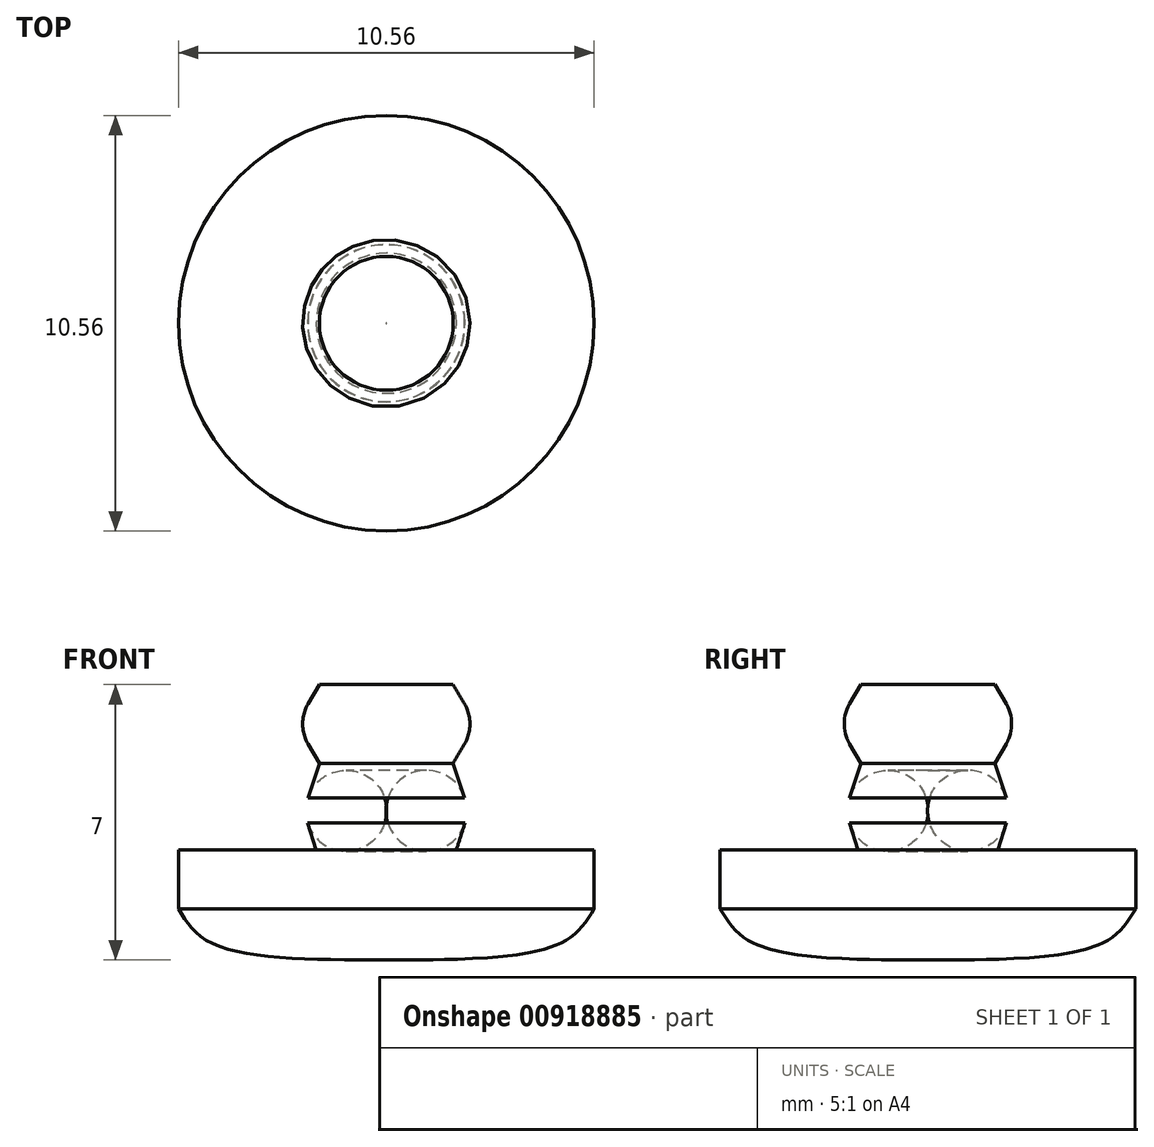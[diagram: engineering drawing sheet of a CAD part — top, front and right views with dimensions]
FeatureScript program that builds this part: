
annotation { "Feature Type Name" : "Feature", "Feature Type Description" : "" }
export const myFeature = defineFeature(function(context is Context, id is Id, definition is map)
    precondition{}
    {
        {
            var Q0;
            Q0=qCreatedBy(makeId("Front.planeOp"),FACE);
            var sketch = newSketch(context, id + "F0", { "sketchPlane" : qUnion([Q0])});
            skLineSegment(sketch, "E0", {"start": v(-34, -22) * mm, "end": v(-34.29, -22.5) * mm});
            skLineSegment(sketch, "E1", {"start": v(-34.29, -23.5) * mm, "end": v(-34, -24) * mm});
            skPoint(sketch, "E2.visualSharp", {"position": v(-34.59, -23) * mm});
            skArc(sketch, "E2.filletArc", {"start": v(-34.29, -22.5) * mm, "mid": v(-34.43, -23) * mm, "end": v(-34.29, -23.5) * mm});
            skLineSegment(sketch, "E3", {"start": v(-34, -24) * mm, "end": v(-34.3, -24.88) * mm});
            skLineSegment(sketch, "E4", {"start": v(-34.3, -25.52) * mm, "end": v(-34.08, -26.2) * mm});
            skPoint(sketch, "E5.visualSharp", {"position": v(-34.4, -25.2) * mm});
            skArc(sketch, "E5.filletArc", {"start": v(-34.3, -24.88) * mm, "mid": v(-34.35, -25.2) * mm, "end": v(-34.3, -25.52) * mm});
            skLineSegment(sketch, "E6", {"start": v(-34.08, -26.2) * mm, "end": v(-37.58, -26.2) * mm});
            skLineSegment(sketch, "E7", {"start": v(-37.58, -26.2) * mm, "end": v(-37.58, -27.7) * mm});
            skFitSpline(sketch, "E8", {"points": [v(-37.58, -27.7) * mm, v(-36.73, -28.57) * mm, v(-32.3, -29) * mm], "startDerivative": vector(1.73, -2.88) * mm, "endDerivative": vector(8.24, -0.02) * mm});
            skLineSegment(sketch, "E9", {"start": v(-34, -22) * mm, "end": v(-32.3, -22) * mm});
            skLineSegment(sketch, "E10", {"start": v(-32.3, -22) * mm, "end": v(-32.3, -29) * mm});
            skSolve(sketch);
        }
        {
            var Q0;
            Q0=makeQuery(id+"F0.imprint","IMPRINT",FACE,{"disambiguationData":[TD([[makeQuery(id+"F0.imprint","IMPRINT",EDGE,{"derivedFrom":sQuery(id+"F0.wireOp",EDGE,"E0")}),1.0]])]});
            var Q1;
            Q1=sQuery(id+"F0.wireOp",EDGE,"E10");
            revolve(context, id + "F1", {"surfaceOperationType" : NewSurfaceOperationType.NEW, "entities" : qUnion([Q0]), "axis" : qUnion([Q1]), "revolveType" : RevolveType.FULL});
        }
    });
